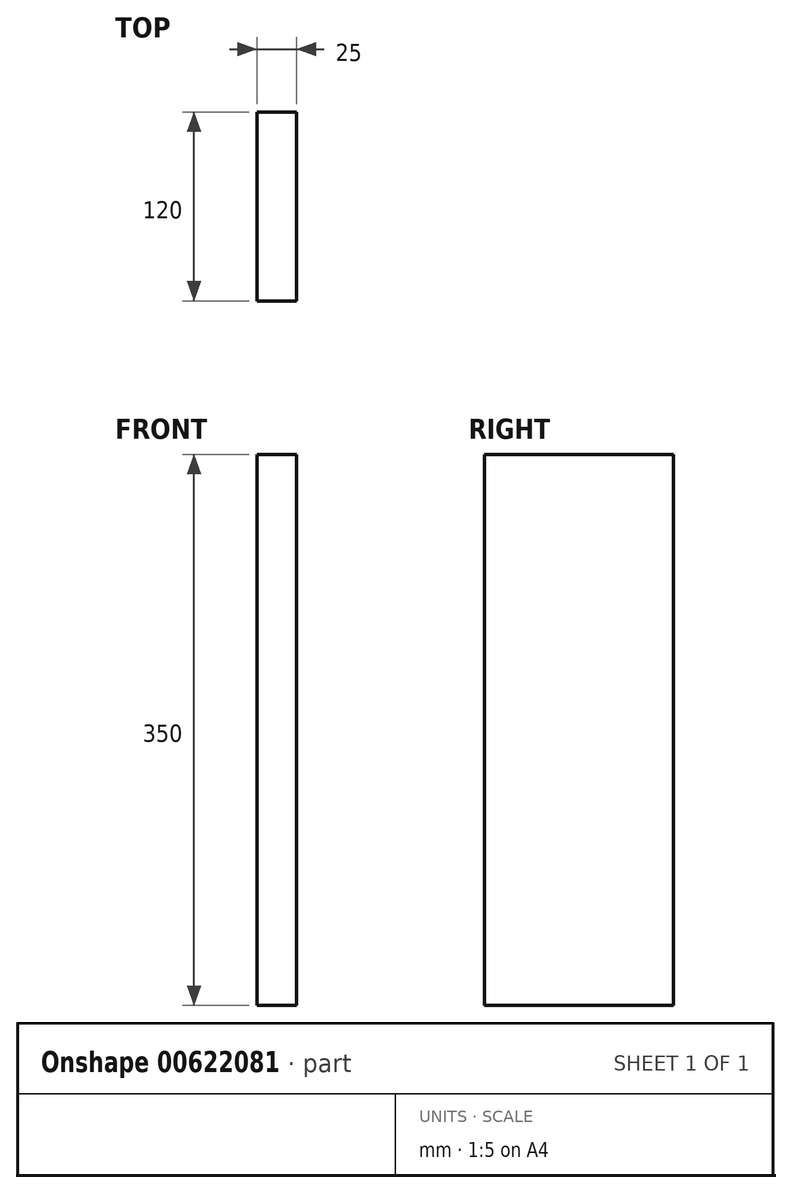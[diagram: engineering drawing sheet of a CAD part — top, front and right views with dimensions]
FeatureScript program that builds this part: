
annotation { "Feature Type Name" : "Feature", "Feature Type Description" : "" }
export const myFeature = defineFeature(function(context is Context, id is Id, definition is map)
    precondition{}
    {
        {
            var Q0;
            Q0=qCreatedBy(makeId("Right.planeOp"),FACE);
            var sketch = newSketch(context, id + "F0", { "sketchPlane" : qUnion([Q0])});
            skLineSegment(sketch, "E0.bottom", {"start": v(-60, 175) * mm, "end": v(60, 175) * mm});
            skLineSegment(sketch, "E0.top", {"start": v(-60, -175) * mm, "end": v(60, -175) * mm});
            skLineSegment(sketch, "E0.left", {"start": v(-60, 175) * mm, "end": v(-60, -175) * mm});
            skLineSegment(sketch, "E0.right", {"start": v(60, 175) * mm, "end": v(60, -175) * mm});
            skPoint(sketch, "E0.middle", {"position": v(0, 0) * mm});
            skSolve(sketch);
        }
        {
            var Q0;
            Q0=makeQuery(id+"F0.imprint","IMPRINT",FACE,{"disambiguationData":[TD([[makeQuery(id+"F0.imprint","IMPRINT",EDGE,{"derivedFrom":sQuery(id+"F0.wireOp",EDGE,"E0.bottom")}),-1.0]])]});
            extrude(context, id + "F1", {"entities" : qUnion([Q0]), "depth" : 25 * mm, "offsetDistance" : 25 * mm});
        }
    });
